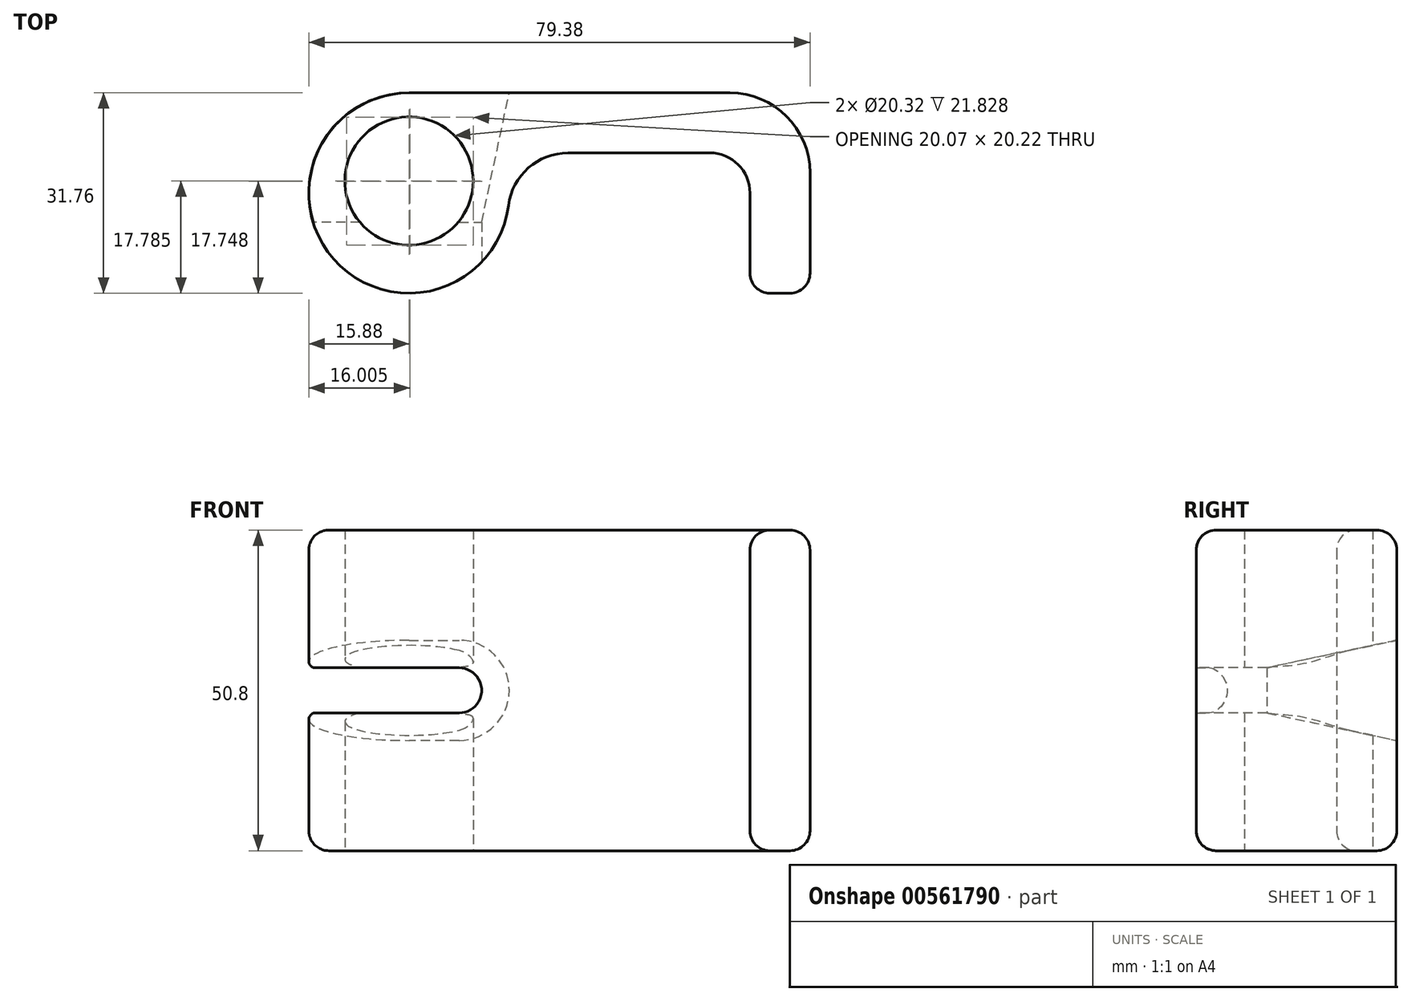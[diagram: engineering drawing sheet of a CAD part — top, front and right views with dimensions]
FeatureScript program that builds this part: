
annotation { "Feature Type Name" : "Feature", "Feature Type Description" : "" }
export const myFeature = defineFeature(function(context is Context, id is Id, definition is map)
    precondition{}
    {
        {
            var Q0;
            Q0=qCreatedBy(makeId("Top.planeOp"),FACE);
            var sketch = newSketch(context, id + "F0", { "sketchPlane" : qUnion([Q0])});
            skCircle(sketch, "E0", {"center": v(0, 0) * mm, "radius": 15.88 * mm});
            skCircle(sketch, "E1", {"center": v(0, 1.9) * mm, "radius": 10.16 * mm});
            skLineSegment(sketch, "E2", {"start": v(0, 15.88) * mm, "end": v(50.8, 15.88) * mm});
            skLineSegment(sketch, "E3", {"start": v(63.5, 3.17) * mm, "end": v(63.5, -12.7) * mm});
            skLineSegment(sketch, "E4", {"start": v(60.33, -15.87) * mm, "end": v(57.15, -15.87) * mm});
            skLineSegment(sketch, "E5", {"start": v(53.98, -12.7) * mm, "end": v(53.98, 0) * mm});
            skLineSegment(sketch, "E6", {"start": v(47.62, 6.35) * mm, "end": v(22.7, 6.35) * mm});
            skPoint(sketch, "E7.visualSharp", {"position": v(53.98, 6.35) * mm});
            skArc(sketch, "E7.filletArc", {"start": v(53.98, 0) * mm, "mid": v(52.12, 4.5) * mm, "end": v(47.62, 6.35) * mm});
            skPoint(sketch, "E8.visualSharp", {"position": v(63.5, 15.88) * mm});
            skArc(sketch, "E8.filletArc", {"start": v(63.5, 3.17) * mm, "mid": v(59.78, 12.16) * mm, "end": v(50.8, 15.88) * mm});
            skCircle(sketch, "E9", {"center": v(25.2, -3.18) * mm, "radius": 9.53 * mm});
            skPoint(sketch, "E10.visualSharp", {"position": v(53.98, -15.87) * mm});
            skArc(sketch, "E10.filletArc", {"start": v(53.98, -12.7) * mm, "mid": v(54.9, -14.95) * mm, "end": v(57.15, -15.87) * mm});
            skPoint(sketch, "E11.visualSharp", {"position": v(63.5, -15.87) * mm});
            skArc(sketch, "E11.filletArc", {"start": v(60.33, -15.87) * mm, "mid": v(62.57, -14.95) * mm, "end": v(63.5, -12.7) * mm});
            skSolve(sketch);
        }
        {
            var Q0;
            {var subQ6=sQuery(id+"F0.wireOp",EDGE,"E2");Q0=makeQuery(id+"F0.imprint","IMPRINT",FACE,{"disambiguationData":[TD([[makeQuery(id+"F0.imprint","IMPRINT",EDGE,{"derivedFrom":subQ6}),-1.0]])]});}
            var Q1;
            Q1=makeQuery(id+"F0.imprint","IMPRINT",FACE,{"disambiguationData":[TD([[makeQuery(id+"F0.imprint","IMPRINT",EDGE,{"derivedFrom":sQuery(id+"F0.wireOp",EDGE,"E1")}),-1.0]])]});
            extrude(context, id + "F1", {"entities" : qUnion([Q0, Q1]), "depth" : 50.8 * mm, "offsetDistance" : 25.4 * mm});
        }
        {
            var Q0;
            Q0=makeQuery(id+"F1.opExtrude","SWEPT_FACE",FACE,{"disambiguationData":[OSD([sQuery(id+"F0.wireOp",EDGE,"E2")])]});
            var sketch = newSketch(context, id + "F2", { "sketchPlane" : qUnion([Q0])});
            skLineSegment(sketch, "E12", {"start": v(0, 50.8) * mm, "end": v(0, 25.4) * mm, "construction": true});
            skLineSegment(sketch, "E13", {"start": v(-7.94, 25.4) * mm, "end": v(36.45, 25.4) * mm, "construction": true});
            skLineSegment(sketch, "E14.0", {"start": v(-7.94, 17.46) * mm, "end": v(38.1, 17.46) * mm});
            skLineSegment(sketch, "E15.0", {"start": v(-7.94, 33.34) * mm, "end": v(38.1, 33.34) * mm});
            skArc(sketch, "E16", {"start": v(-7.94, 33.34) * mm, "mid": v(-15.87, 25.4) * mm, "end": v(-7.94, 17.46) * mm});
            skPoint(sketch, "E17", {"position": v(0, 25.4) * mm});
            skLineSegment(sketch, "E18", {"start": v(38.1, 33.34) * mm, "end": v(38.1, 17.46) * mm});
            skPoint(sketch, "E19.orphan", {"position": v(0, 0) * mm});
            skSolve(sketch);
        }
        {
            var Q0;
            Q0=makeQuery(id+"F1.opExtrude","CAP_EDGE",EDGE,{"disambiguationData":[OSD([sQuery(id+"F0.wireOp",EDGE,"E2")])],"isStart":true});
            var Q1;
            Q1=makeQuery(id+"F1.opExtrude","CAP_EDGE",EDGE,{"disambiguationData":[OSD([sQuery(id+"F0.wireOp",EDGE,"E2")])],"isStart":false});
            fillet(context, id + "F3", {"entities" : qUnion([Q0, Q1]), "radius" : 3.17 * mm, "tangentPropagation" : true, "allowEdgeOverflow" : false});
        }
        {
            var Q0;
            Q0=makeQuery(id+"F1.opExtrude","SWEPT_FACE",FACE,{"disambiguationData":[OSD([sQuery(id+"F0.wireOp",EDGE,"E4")])]});
            var sketch = newSketch(context, id + "F4", { "sketchPlane" : qUnion([Q0])});
            skArc(sketch, "E20", {"start": v(7.94, 21.83) * mm, "mid": v(11.5, 25.4) * mm, "end": v(7.94, 28.97) * mm});
            skLineSegment(sketch, "E21", {"start": v(7.94, 28.97) * mm, "end": v(-38.1, 28.97) * mm});
            skLineSegment(sketch, "E22", {"start": v(-38.1, 28.97) * mm, "end": v(-38.1, 21.83) * mm});
            skLineSegment(sketch, "E23", {"start": v(7.94, 21.83) * mm, "end": v(-38.1, 21.83) * mm});
            skSolve(sketch);
        }
        {
            var Q0;
            {var subQ0=sQuery(id+"F2.wireOp",EDGE,"E16");Q0=makeQuery(id+"F2.imprint","IMPRINT",FACE,{"disambiguationData":[TD([[makeQuery(id+"F2.imprint","IMPRINT",EDGE,{"derivedFrom":subQ0}),1.0]])]});}
            var Q1;
            {var subQ0=sQuery(id+"F2.wireOp",EDGE,"E18");Q1=makeQuery(id+"F2.imprint","IMPRINT",FACE,{"disambiguationData":[TD([[makeQuery(id+"F2.imprint","IMPRINT",EDGE,{"derivedFrom":subQ0}),-1.0]])]});}
            extrude(context, id + "F5", {"entities" : qUnion([Q0, Q1]), "operationType" : NewBodyOperationType.REMOVE, "endBound" : BoundingType.THROUGH_ALL, "oppositeDirection" : true, "depth" : 25.4 * mm, "offsetDistance" : 25.4 * mm, "hasDraft" : true, "draftAngle" : 12 * degree, "draftPullDirection" : true});
        }
        {
            var Q0;
            Q0=makeQuery(id+"F4.imprint","IMPRINT",FACE,{"disambiguationData":[TD([[makeQuery(id+"F4.imprint","IMPRINT",EDGE,{"derivedFrom":sQuery(id+"F4.wireOp",EDGE,"E20")}),1.0]])]});
            extrude(context, id + "F6", {"entities" : qUnion([Q0]), "operationType" : NewBodyOperationType.REMOVE, "oppositeDirection" : true, "depth" : 25.4 * mm, "offsetDistance" : 25.4 * mm});
        }
    });
